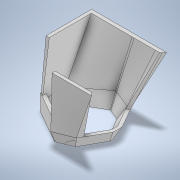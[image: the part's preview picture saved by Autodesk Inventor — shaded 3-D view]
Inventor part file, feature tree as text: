
AUTODESK INVENTOR PART (.ipt)
format: ipt  version: 2022 (Build 260153000, 153)  size: 331,264 bytes
history: native  units: in
note: dims shown in document units (in); Inventor stores cm internally (conversion verified against a paired STEP export)
features: sketch x6, plane x4, loft x3, extrude x1, split x1
ambient origin geometry x8: Origin, YZ Plane, XZ Plane, XY Plane, X Axis, Y Axis, Z Axis, Center Point
bodies: Solid1 (feature_tree)
feature tree (15):
  sketch  "Sketch1"  dims[d0=0.2441in d1=60.0deg]
  plane  "Work Plane1"
  plane  "Work Plane2"
  sketch  "Sketch2"  dims[d2=0.1063in d3=0.202in]
  loft  "Loft1"
  extrude  "Extrusion3"  Depth=0.202in
  sketch  "Sketch4"  dims[d8=0.0315in d11=0.1181in]
  plane  "Work Plane3"
  split  "Split3"
  sketch  "Sketch5"  dims[d14=0.0315in]
  plane  "Work Plane4"
  sketch  "Sketch6"  dims[d15=0.0315in d16=0.0in d17=90.0deg d18=0.0in d19=90.0deg d20=0.1181in d27=0.0394in d28=0.1181in d29=0.0in d30=0.0in d31=-0.0276in d33=0.3937in d34=0.4331in d36=0.0315in d39=0.0315in d40=0.6299in d44=0.3543in d45=0.7087in d48=0.0315in d57=0.0in d58=90.0deg d59=0.0in d60=90.0deg d61=0.0in d62=90.0deg d63=0.0in d64=90.0deg]
  loft  "Loft3"
  loft  "Loft4"
  sketch  "Sketch3"  dims[d4=0.1181in d7=0.0315in]
